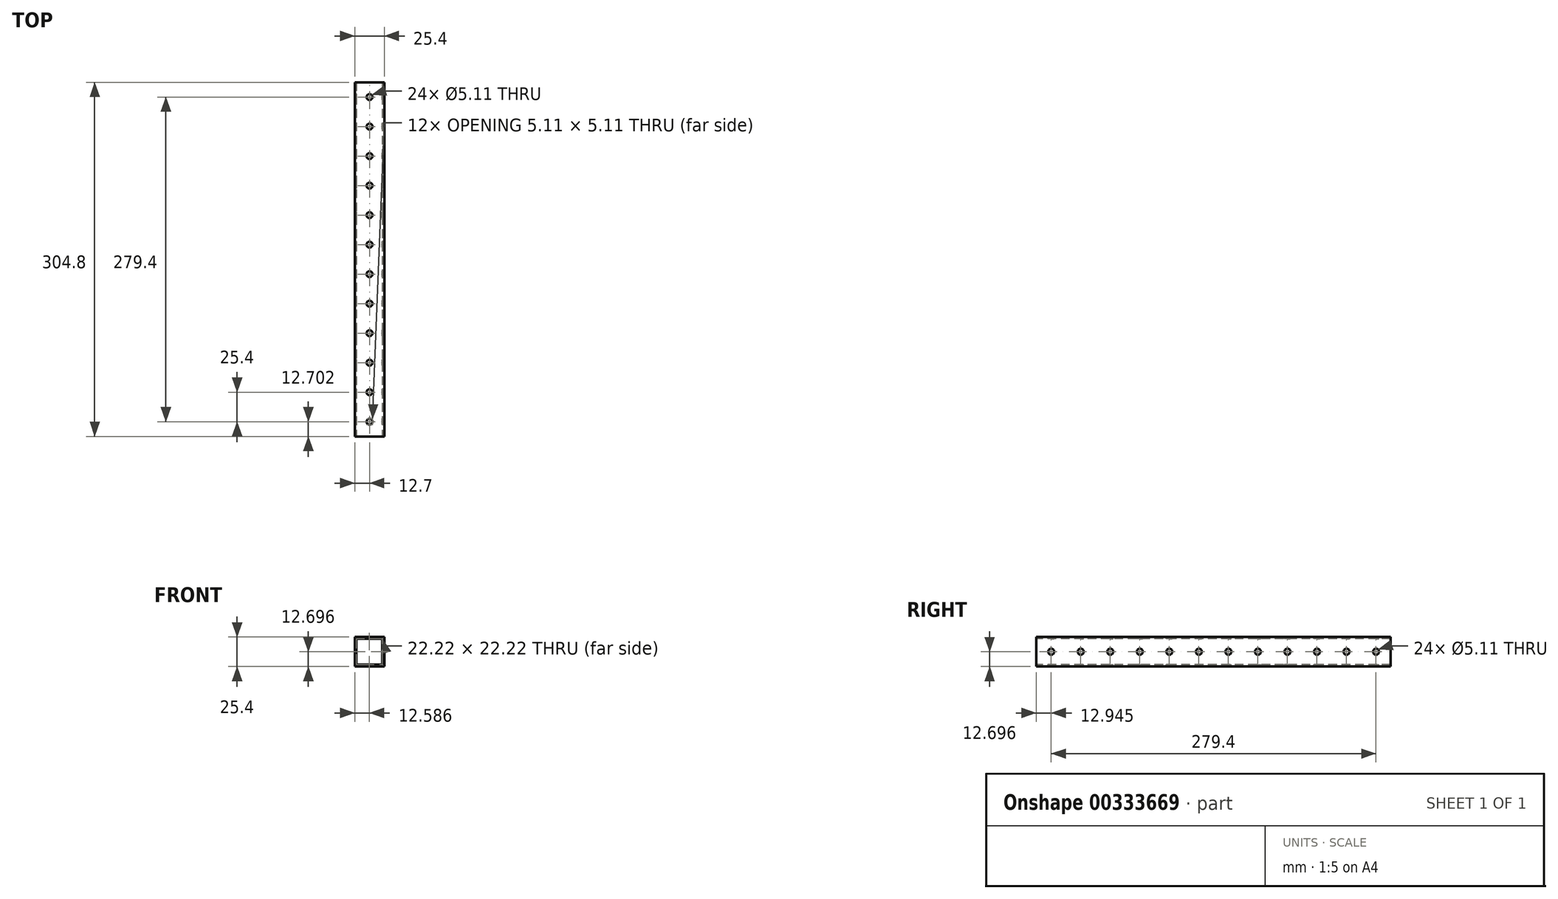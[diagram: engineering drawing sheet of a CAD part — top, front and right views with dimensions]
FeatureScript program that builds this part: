
annotation { "Feature Type Name" : "Feature", "Feature Type Description" : "" }
export const myFeature = defineFeature(function(context is Context, id is Id, definition is map)
    precondition{}
    {
        {
            var Q0;
            Q0=qCreatedBy(makeId("Right.planeOp"),FACE);
            var sketch = newSketch(context, id + "F0", { "sketchPlane" : qUnion([Q0])});
            skLineSegment(sketch, "E0.bottom", {"start": v(-73.53, 30.22) * mm, "end": v(231.27, 30.22) * mm});
            skLineSegment(sketch, "E0.top", {"start": v(-73.53, 4.82) * mm, "end": v(231.27, 4.82) * mm});
            skLineSegment(sketch, "E0.left", {"start": v(-73.53, 30.22) * mm, "end": v(-73.53, 4.82) * mm});
            skLineSegment(sketch, "E0.right", {"start": v(231.27, 30.22) * mm, "end": v(231.27, 4.82) * mm});
            skSolve(sketch);
        }
        {
            var Q0;
            Q0=makeQuery(id+"F0.imprint","IMPRINT",FACE,{"disambiguationData":[TD([[makeQuery(id+"F0.imprint","IMPRINT",EDGE,{"derivedFrom":sQuery(id+"F0.wireOp",EDGE,"E0.bottom")}),-1.0]])]});
            extrude(context, id + "F1", {"entities" : qUnion([Q0]), "depth" : 25.4 * mm});
        }
        {
            var Q0;
            Q0=makeQuery(id+"F1.opExtrude","SWEPT_FACE",FACE,{"disambiguationData":[OSD([sQuery(id+"F0.wireOp",EDGE,"E0.left")])]});
            var sketch = newSketch(context, id + "F2", { "sketchPlane" : qUnion([Q0])});
            skLineSegment(sketch, "E1.bottom", {"start": v(1.47, 28.63) * mm, "end": v(23.7, 28.63) * mm});
            skLineSegment(sketch, "E1.top", {"start": v(1.47, 6.4) * mm, "end": v(23.7, 6.4) * mm});
            skLineSegment(sketch, "E1.left", {"start": v(1.47, 28.63) * mm, "end": v(1.47, 6.4) * mm});
            skLineSegment(sketch, "E1.right", {"start": v(23.7, 28.63) * mm, "end": v(23.7, 6.4) * mm});
            skPoint(sketch, "E1.middle", {"position": v(12.59, 17.52) * mm});
            skPoint(sketch, "E1.middle.positionSnap0", {"position": v(0, 17.52) * mm});
            skPoint(sketch, "E1.centerSnap0", {"position": v(0, 17.52) * mm});
            skSolve(sketch);
        }
        {
            var Q0;
            Q0=makeQuery(id+"F2.imprint","IMPRINT",FACE,{"disambiguationData":[TD([[makeQuery(id+"F2.imprint","IMPRINT",EDGE,{"derivedFrom":sQuery(id+"F2.wireOp",EDGE,"E1.bottom")}),-1.0]])]});
            extrude(context, id + "F3", {"entities" : qUnion([Q0]), "operationType" : NewBodyOperationType.REMOVE, "oppositeDirection" : true, "depth" : 304.8 * mm});
        }
        {
            var Q0;
            Q0=makeQuery(id+"F1.opExtrude","SWEPT_FACE",FACE,{"disambiguationData":[OSD([sQuery(id+"F0.wireOp",EDGE,"E0.bottom")])]});
            var sketch = newSketch(context, id + "F4", { "sketchPlane" : qUnion([Q0])});
            skCircle(sketch, "E2", {"center": v(12.7, -60.83) * mm, "radius": 2.55 * mm});
            skCircle(sketch, "E3.0.1.0", {"center": v(12.7, -35.43) * mm, "radius": 2.55 * mm});
            skCircle(sketch, "E3.0.2.0", {"center": v(12.7, -10.03) * mm, "radius": 2.55 * mm});
            skCircle(sketch, "E3.0.3.0", {"center": v(12.7, 15.37) * mm, "radius": 2.55 * mm});
            skCircle(sketch, "E3.0.4.0", {"center": v(12.7, 40.77) * mm, "radius": 2.55 * mm});
            skCircle(sketch, "E3.0.5.0", {"center": v(12.7, 66.17) * mm, "radius": 2.55 * mm});
            skCircle(sketch, "E3.0.6.0", {"center": v(12.7, 91.57) * mm, "radius": 2.55 * mm});
            skCircle(sketch, "E3.0.7.0", {"center": v(12.7, 116.97) * mm, "radius": 2.55 * mm});
            skCircle(sketch, "E3.0.8.0", {"center": v(12.7, 142.37) * mm, "radius": 2.55 * mm});
            skCircle(sketch, "E3.0.9.0", {"center": v(12.7, 167.77) * mm, "radius": 2.55 * mm});
            skCircle(sketch, "E3.0.10.0", {"center": v(12.7, 193.17) * mm, "radius": 2.55 * mm});
            skCircle(sketch, "E3.0.11.0", {"center": v(12.7, 218.57) * mm, "radius": 2.55 * mm});
            skLineSegment(sketch, "E3.direction1", {"start": v(12.7, -60.83) * mm, "end": v(38.1, -60.83) * mm, "construction": true});
            skLineSegment(sketch, "E3.direction2", {"start": v(12.7, -60.83) * mm, "end": v(12.7, -35.43) * mm, "construction": true});
            skSolve(sketch);
        }
        {
            var Q0;
            Q0 = qSketchRegion(id + "F4", true);
            extrude(context, id + "F5", {"entities" : qUnion([Q0]), "operationType" : NewBodyOperationType.REMOVE, "oppositeDirection" : true, "depth" : 25.4 * mm});
        }
        {
            var Q0;
            Q0=makeQuery(id+"F1.opExtrude","CAP_FACE",FACE,{"disambiguationData":[OSD([sQuery(id+"F0.wireOp",EDGE,"E0.bottom"),sQuery(id+"F0.wireOp",EDGE,"E0.top"),sQuery(id+"F0.wireOp",EDGE,"E0.left"),sQuery(id+"F0.wireOp",EDGE,"E0.right")])],"isStart":true});
            var sketch = newSketch(context, id + "F6", { "sketchPlane" : qUnion([Q0])});
            skCircle(sketch, "E4", {"center": v(60.58, 17.52) * mm, "radius": 2.55 * mm});
            skCircle(sketch, "E5.1.0.0", {"center": v(35.18, 17.52) * mm, "radius": 2.55 * mm});
            skCircle(sketch, "E5.2.0.0", {"center": v(9.78, 17.52) * mm, "radius": 2.55 * mm});
            skCircle(sketch, "E5.3.0.0", {"center": v(-15.62, 17.52) * mm, "radius": 2.55 * mm});
            skCircle(sketch, "E5.4.0.0", {"center": v(-41.02, 17.52) * mm, "radius": 2.55 * mm});
            skCircle(sketch, "E5.5.0.0", {"center": v(-66.42, 17.52) * mm, "radius": 2.55 * mm});
            skCircle(sketch, "E5.6.0.0", {"center": v(-91.82, 17.52) * mm, "radius": 2.55 * mm});
            skCircle(sketch, "E5.7.0.0", {"center": v(-117.22, 17.52) * mm, "radius": 2.55 * mm});
            skCircle(sketch, "E5.8.0.0", {"center": v(-142.62, 17.52) * mm, "radius": 2.55 * mm});
            skCircle(sketch, "E5.9.0.0", {"center": v(-168.02, 17.52) * mm, "radius": 2.55 * mm});
            skCircle(sketch, "E5.10.0.0", {"center": v(-193.42, 17.52) * mm, "radius": 2.55 * mm});
            skCircle(sketch, "E5.11.0.0", {"center": v(-218.82, 17.52) * mm, "radius": 2.55 * mm});
            skLineSegment(sketch, "E5.direction1", {"start": v(60.58, 17.52) * mm, "end": v(35.18, 17.52) * mm, "construction": true});
            skSolve(sketch);
        }
        {
            var Q0;
            Q0 = qSketchRegion(id + "F6", true);
            extrude(context, id + "F7", {"entities" : qUnion([Q0]), "operationType" : NewBodyOperationType.REMOVE, "oppositeDirection" : true, "depth" : 25.4 * mm});
        }
    });
